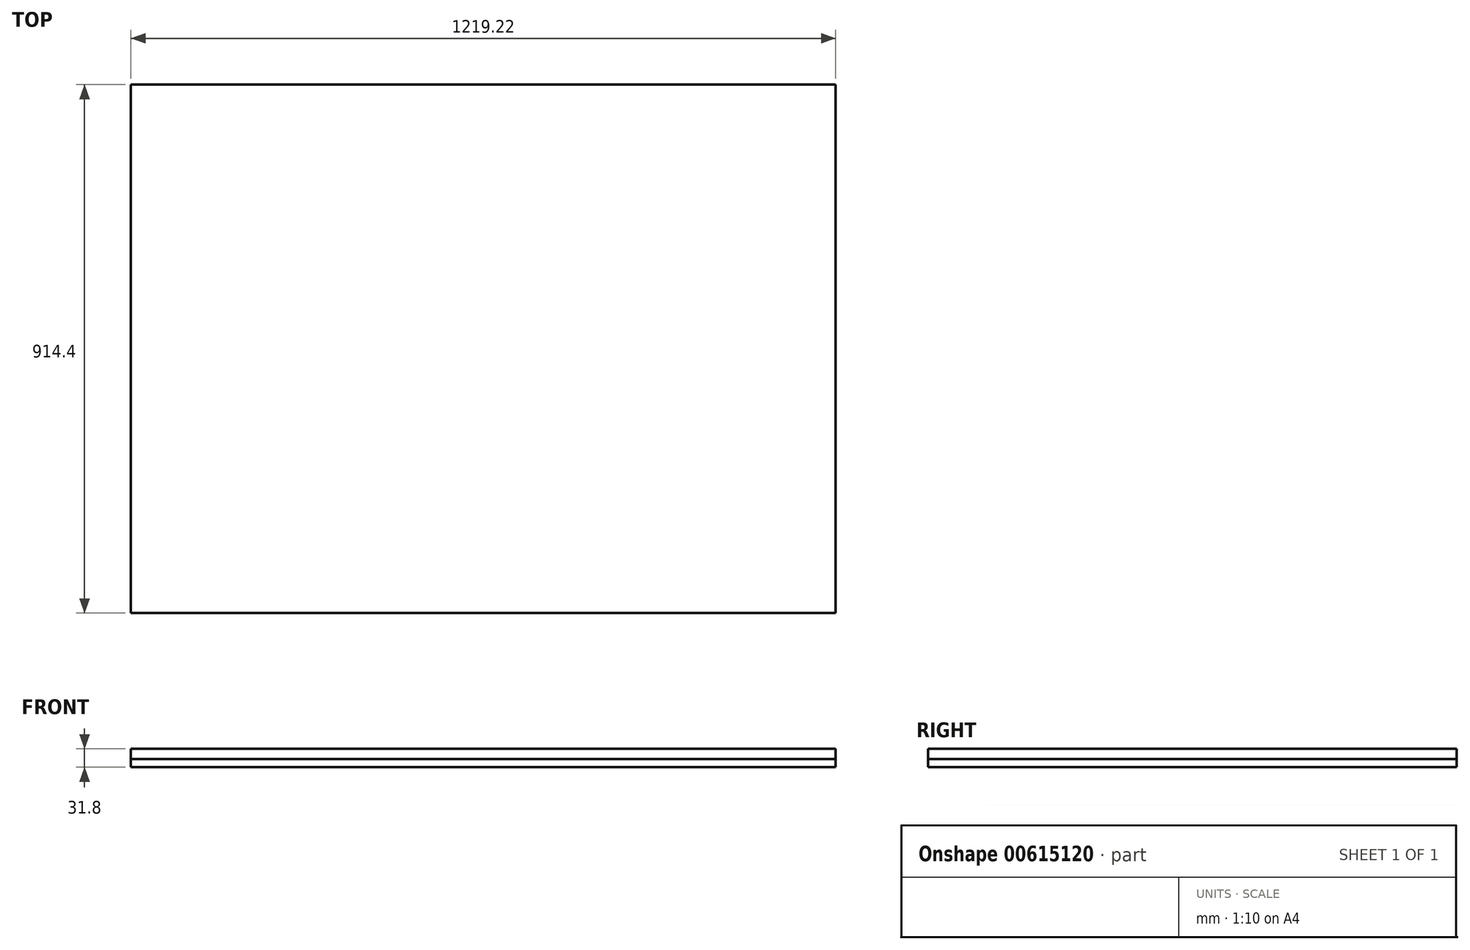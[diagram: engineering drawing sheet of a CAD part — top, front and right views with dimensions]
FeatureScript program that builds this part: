
annotation { "Feature Type Name" : "Feature", "Feature Type Description" : "" }
export const myFeature = defineFeature(function(context is Context, id is Id, definition is map)
    precondition{}
    {
        {
            var Q0;
            Q0=qCreatedBy(makeId("Front.planeOp"),FACE);
            var sketch = newSketch(context, id + "F0", { "sketchPlane" : qUnion([Q0])});
            skLineSegment(sketch, "E0.bottom", {"start": v(-586.04, 27.92) * mm, "end": v(633.16, 27.92) * mm});
            skLineSegment(sketch, "E0.top", {"start": v(-586.04, 10.14) * mm, "end": v(633.16, 10.14) * mm});
            skLineSegment(sketch, "E0.left", {"start": v(-586.04, 27.92) * mm, "end": v(-586.04, 10.14) * mm});
            skLineSegment(sketch, "E0.right", {"start": v(633.16, 27.92) * mm, "end": v(633.16, 10.14) * mm});
            skLineSegment(sketch, "E1.bottom", {"start": v(-586.06, 10.34) * mm, "end": v(633.14, 10.34) * mm});
            skLineSegment(sketch, "E1.top", {"start": v(-586.06, -3.88) * mm, "end": v(633.14, -3.88) * mm});
            skLineSegment(sketch, "E1.left", {"start": v(-586.06, 10.34) * mm, "end": v(-586.06, -3.88) * mm});
            skLineSegment(sketch, "E1.right", {"start": v(633.14, 10.34) * mm, "end": v(633.14, -3.88) * mm});
            skSolve(sketch);
        }
        {
            var Q0;
            {var subQ2=sQuery(id+"F0.wireOp",EDGE,"E0.bottom");Q0=makeQuery(id+"F0.imprint","IMPRINT",FACE,{"disambiguationData":[TD([[makeQuery(id+"F0.imprint","IMPRINT",EDGE,{"derivedFrom":subQ2}),-1.0]])]});}
            var Q1;
            {var subQ0=sQuery(id+"F0.wireOp",EDGE,"E1.top");Q1=makeQuery(id+"F0.imprint","IMPRINT",FACE,{"disambiguationData":[TD([[makeQuery(id+"F0.imprint","IMPRINT",EDGE,{"derivedFrom":subQ0}),1.0]])]});}
            extrude(context, id + "F1", {"entities" : qUnion([Q0, Q1]), "depth" : 914.4 * mm});
        }
    });
